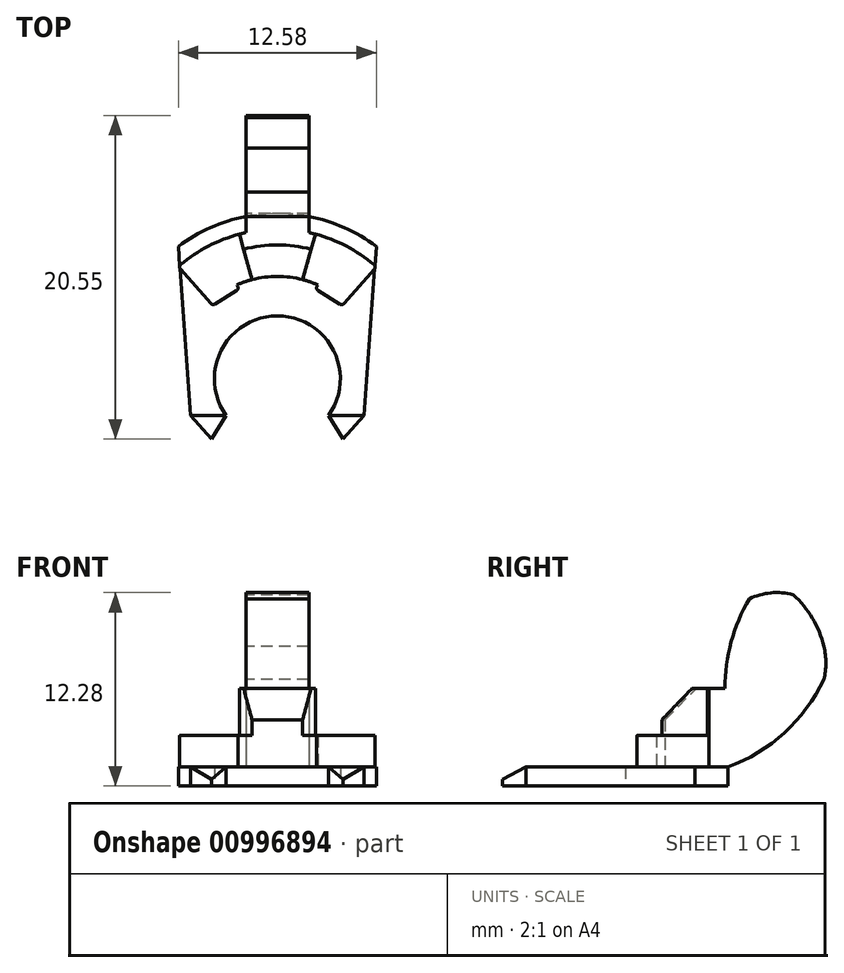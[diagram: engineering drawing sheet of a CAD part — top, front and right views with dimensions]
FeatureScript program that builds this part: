
annotation { "Feature Type Name" : "Feature", "Feature Type Description" : "" }
export const myFeature = defineFeature(function(context is Context, id is Id, definition is map)
    precondition{}
    {
        {
            var Q0;
            Q0=qCreatedBy(makeId("Top.planeOp"),FACE);
            var sketch = newSketch(context, id + "F0", { "sketchPlane" : qUnion([Q0])});
            skLineSegment(sketch, "E0", {"start": v(-7.13, -2.33) * mm, "end": v(-5.5, -2.33) * mm, "construction": true});
            skLineSegment(sketch, "E1", {"start": v(-3.25, -2.33) * mm, "end": v(3.25, -2.33) * mm, "construction": true});
            skLineSegment(sketch, "E2", {"start": v(3.25, -2.33) * mm, "end": v(5.5, -2.33) * mm, "construction": true});
            skArc(sketch, "E3", {"start": v(-7.13, -2.33) * mm, "mid": v(0, -7.5) * mm, "end": v(7.13, -2.33) * mm, "construction": true});
            skArc(sketch, "E4", {"start": v(7.13, -2.33) * mm, "mid": v(7.4, 1.22) * mm, "end": v(6, 4.5) * mm, "construction": true});
            skArc(sketch, "E5", {"start": v(3.25, -2.33) * mm, "mid": v(0, 4) * mm, "end": v(-3.25, -2.33) * mm});
            skArc(sketch, "E6", {"start": v(-3.25, -2.33) * mm, "mid": v(0, -4) * mm, "end": v(3.25, -2.33) * mm, "construction": true});
            skLineSegment(sketch, "E7", {"start": v(-6, 4.5) * mm, "end": v(6, 4.5) * mm, "construction": true});
            skArc(sketch, "E8", {"start": v(6, 4.5) * mm, "mid": v(0, 7.5) * mm, "end": v(-6, 4.5) * mm, "construction": true});
            skArc(sketch, "E9", {"start": v(-6, 4.5) * mm, "mid": v(-7.4, 1.22) * mm, "end": v(-7.13, -2.33) * mm, "construction": true});
            skLineSegment(sketch, "E10", {"start": v(-6.29, 8.41) * mm, "end": v(-5.5, -2.33) * mm});
            skLineSegment(sketch, "E11", {"start": v(6.29, 8.41) * mm, "end": v(5.5, -2.33) * mm});
            skLineSegment(sketch, "E12", {"start": v(-5.5, -2.33) * mm, "end": v(-3.25, -2.33) * mm, "construction": true});
            skLineSegment(sketch, "E13", {"start": v(5.5, -2.33) * mm, "end": v(7.13, -2.33) * mm, "construction": true});
            skLineSegment(sketch, "E14", {"start": v(-5.5, -2.33) * mm, "end": v(-4.18, -3.83) * mm});
            skLineSegment(sketch, "E15", {"start": v(-4.18, -3.83) * mm, "end": v(-3.25, -2.33) * mm});
            skLineSegment(sketch, "E16", {"start": v(3.25, -2.33) * mm, "end": v(4.18, -3.83) * mm});
            skLineSegment(sketch, "E17", {"start": v(4.18, -3.83) * mm, "end": v(5.5, -2.33) * mm});
            skArc(sketch, "E18", {"start": v(-6.29, 8.41) * mm, "mid": v(0, 10.5) * mm, "end": v(6.29, 8.41) * mm});
            skPoint(sketch, "E19", {"position": v(0, 10.5) * mm});
            skPoint(sketch, "E20", {"position": v(0, 7.5) * mm});
            skSolve(sketch);
        }
        {
            var Q0;
            Q0=qSketchRegion(id+"F0",true);
            extrude(context, id + "F1", {"entities" : qUnion([Q0]), "depth" : 1.2 * mm});
        }
        {
            var Q0;
            Q0=qCreatedBy(makeId("Right.planeOp"),FACE);
            var sketch = newSketch(context, id + "F2", { "sketchPlane" : qUnion([Q0])});
            skPoint(sketch, "E21.0", {"position": v(-2.33, 1.2) * mm});
            skLineSegment(sketch, "E22", {"start": v(-2.33, 1.2) * mm, "end": v(-3.83, 0.4) * mm});
            skLineSegment(sketch, "E23", {"start": v(-3.83, 0.4) * mm, "end": v(-3.83, 1.2) * mm});
            skLineSegment(sketch, "E24", {"start": v(-2.33, 1.2) * mm, "end": v(-3.83, 1.2) * mm});
            skSolve(sketch);
        }
        {
            var Q0;
            Q0=qSketchRegion(id+"F2",true);
            extrude(context, id + "F3", {"entities" : qUnion([Q0]), "operationType" : NewBodyOperationType.REMOVE, "endBound" : BoundingType.SYMMETRIC, "oppositeDirection" : true, "depth" : 25 * mm});
        }
        {
            var Q0;
            Q0=makeQuery(id+"F1.opExtrude","CAP_FACE",FACE,{"disambiguationData":[OSD([sQuery(id+"F0.wireOp",EDGE,"E5"),sQuery(id+"F0.wireOp",EDGE,"E10"),sQuery(id+"F0.wireOp",EDGE,"E11"),sQuery(id+"F0.wireOp",EDGE,"E14"),sQuery(id+"F0.wireOp",EDGE,"E15"),sQuery(id+"F0.wireOp",EDGE,"E16"),sQuery(id+"F0.wireOp",EDGE,"E17"),sQuery(id+"F0.wireOp",EDGE,"E18")])],"isStart":false});
            var sketch = newSketch(context, id + "F4", { "sketchPlane" : qUnion([Q0])});
            skArc(sketch, "E25.0", {"start": v(0, 9.5) * mm, "mid": v(-3.27, 8.92) * mm, "end": v(-6.14, 7.25) * mm});
            skArc(sketch, "E26.0", {"start": v(0, 6.5) * mm, "mid": v(-1.31, 6.37) * mm, "end": v(-2.58, 5.97) * mm});
            skPoint(sketch, "E27", {"position": v(0, 9.5) * mm});
            skPoint(sketch, "E28", {"position": v(0, 6.5) * mm});
            skLineSegment(sketch, "E29", {"start": v(-6.3, 7.12) * mm, "end": v(-6.71, 6.74) * mm, "construction": true});
            skLineSegment(sketch, "E30", {"start": v(-6.16, 6.97) * mm, "end": v(-4.3, 4.87) * mm});
            skLineSegment(sketch, "E31", {"start": v(-4.3, 4.87) * mm, "end": v(-4.22, 4.77) * mm});
            skLineSegment(sketch, "E32", {"start": v(-3.96, 4.74) * mm, "end": v(-2.58, 5.6) * mm});
            skLineSegment(sketch, "E33", {"start": v(-2.52, 5.88) * mm, "end": v(-2.58, 5.97) * mm});
            skLineSegment(sketch, "E34", {"start": v(0, 9.5) * mm, "end": v(0, 6.5) * mm, "construction": true});
            skPoint(sketch, "E35.start.orphan", {"position": v(3.7, 8.75) * mm});
            skPoint(sketch, "E36.visualSharp", {"position": v(-6.3, 7.12) * mm});
            skArc(sketch, "E36.filletArc", {"start": v(-6.14, 7.25) * mm, "mid": v(-6.2, 7.11) * mm, "end": v(-6.16, 6.97) * mm});
            skPoint(sketch, "E37.visualSharp", {"position": v(-4.1, 4.65) * mm});
            skArc(sketch, "E37.filletArc", {"start": v(-4.22, 4.77) * mm, "mid": v(-4.1, 4.7) * mm, "end": v(-3.96, 4.74) * mm});
            skPoint(sketch, "E38.visualSharp", {"position": v(-2.41, 5.71) * mm});
            skArc(sketch, "E38.filletArc", {"start": v(-2.58, 5.6) * mm, "mid": v(-2.5, 5.73) * mm, "end": v(-2.52, 5.88) * mm});
            skLineSegment(sketch, "E39.MirrorCS", {"start": v(4.3, 4.87) * mm, "end": v(4.22, 4.77) * mm});
            skArc(sketch, "E40.MirrorCS", {"start": v(4.22, 4.77) * mm, "mid": v(4.1, 4.7) * mm, "end": v(3.96, 4.74) * mm});
            skLineSegment(sketch, "E41.MirrorCS", {"start": v(3.96, 4.74) * mm, "end": v(2.58, 5.6) * mm});
            skPoint(sketch, "E42.MirrorP", {"position": v(4.1, 4.65) * mm});
            skLineSegment(sketch, "E43.MirrorCS", {"start": v(6.16, 6.97) * mm, "end": v(4.3, 4.87) * mm});
            skArc(sketch, "E44.MirrorCS", {"start": v(0, 9.5) * mm, "mid": v(3.27, 8.92) * mm, "end": v(6.14, 7.25) * mm});
            skLineSegment(sketch, "E45.MirrorCS", {"start": v(2.52, 5.88) * mm, "end": v(2.58, 5.97) * mm});
            skArc(sketch, "E46.MirrorCS", {"start": v(2.58, 5.6) * mm, "mid": v(2.5, 5.73) * mm, "end": v(2.52, 5.88) * mm});
            skArc(sketch, "E47.MirrorCS", {"start": v(6.14, 7.25) * mm, "mid": v(6.2, 7.11) * mm, "end": v(6.16, 6.97) * mm});
            skArc(sketch, "E48.MirrorCS", {"start": v(0, 6.5) * mm, "mid": v(1.31, 6.37) * mm, "end": v(2.58, 5.97) * mm});
            skPoint(sketch, "E49.MirrorP", {"position": v(6.3, 7.12) * mm});
            skPoint(sketch, "E50.MirrorP", {"position": v(2.41, 5.71) * mm});
            skLineSegment(sketch, "E51", {"start": v(0, 6.5) * mm, "end": v(0, 9.5) * mm});
            skLineSegment(sketch, "E52", {"start": v(1.6, 6.3) * mm, "end": v(2.41, 9.19) * mm});
            skLineSegment(sketch, "E53.MirrorCS", {"start": v(-1.6, 6.3) * mm, "end": v(-2.41, 9.19) * mm});
            skPoint(sketch, "E54.oppositeSnap0", {"position": v(0, 10.5) * mm});
            skLineSegment(sketch, "E54.top", {"start": v(-2, 10.31) * mm, "end": v(0, 10.31) * mm});
            skLineSegment(sketch, "E54.left", {"start": v(-2, 9.29) * mm, "end": v(-2, 10.31) * mm});
            skLineSegment(sketch, "E54.right", {"start": v(0, 9.49) * mm, "end": v(0, 10.31) * mm});
            skLineSegment(sketch, "E55.MirrorCS", {"start": v(2, 9.29) * mm, "end": v(2, 10.31) * mm});
            skLineSegment(sketch, "E56.MirrorCS", {"start": v(2, 10.31) * mm, "end": v(0, 10.31) * mm});
            skSolve(sketch);
        }
        {
            var Q0;
            Q0=qSketchRegion(id+"F4",true);
            extrude(context, id + "F5", {"entities" : qUnion([Q0]), "operationType" : NewBodyOperationType.ADD, "offsetDistance" : 25 * mm, "depth" : 2 * mm});
        }
        {
            var Q0;
            {var subQ0=sQuery(id+"F4.wireOp",EDGE,"E51");Q0=makeQuery(id+"F4.imprint","IMPRINT",FACE,{"disambiguationData":[TD([[makeQuery(id+"F4.imprint","IMPRINT",EDGE,{"derivedFrom":subQ0}),-1.0]])]});}
            var Q1;
            {var subQ0=sQuery(id+"F4.wireOp",EDGE,"E51");Q1=makeQuery(id+"F4.imprint","IMPRINT",FACE,{"disambiguationData":[TD([[makeQuery(id+"F4.imprint","IMPRINT",EDGE,{"derivedFrom":subQ0}),1.0]])]});}
            extrude(context, id + "F6", {"entities" : qUnion([Q0, Q1]), "operationType" : NewBodyOperationType.ADD, "depth" : 5 * mm, "offsetDistance" : 25 * mm});
        }
        {
            var Q0;
            Q0=makeQuery(id+"F6.opExtrude","CAP_EDGE",EDGE,{"disambiguationData":[OSD([sQuery(id+"F4.wireOp",EDGE,"E26.0"),sQuery(id+"F4.wireOp",EDGE,"E48.MirrorCS")])],"isStart":false});
            chamfer(context, id + "F7", {"entities" : qUnion([Q0]), "width" : 2 * mm, "tangentPropagation" : true});
        }
        {
            var Q0;
            {var subQ3=sQuery(id+"F4.wireOp",EDGE,"E55.MirrorCS");Q0=makeQuery(id+"F4.imprint","IMPRINT",FACE,{"disambiguationData":[TD([[makeQuery(id+"F4.imprint","IMPRINT",EDGE,{"derivedFrom":subQ3}),1.0]])]});}
            var Q1;
            {var subQ4=sQuery(id+"F4.wireOp",EDGE,"E54.top");Q1=makeQuery(id+"F4.imprint","IMPRINT",FACE,{"disambiguationData":[TD([[makeQuery(id+"F4.imprint","IMPRINT",EDGE,{"derivedFrom":subQ4}),-1.0]])]});}
            var Q2;
            Q2=makeQuery(id+"F6.opExtrude","CAP_FACE",FACE,{"disambiguationData":[OSD([sQuery(id+"F4.wireOp",EDGE,"E25.0"),sQuery(id+"F4.wireOp",EDGE,"E26.0"),sQuery(id+"F4.wireOp",EDGE,"E44.MirrorCS"),sQuery(id+"F4.wireOp",EDGE,"E48.MirrorCS"),sQuery(id+"F4.wireOp",EDGE,"E52"),sQuery(id+"F4.wireOp",EDGE,"E53.MirrorCS")])],"isStart":false});
            var Q3;
            Q3=makeQuery(id+"F1.opExtrude","SWEPT_BODY",BODY,{"disambiguationData":[OSD([sQuery(id+"F0.wireOp",EDGE,"E5"),sQuery(id+"F0.wireOp",EDGE,"E10"),sQuery(id+"F0.wireOp",EDGE,"E11"),sQuery(id+"F0.wireOp",EDGE,"E14"),sQuery(id+"F0.wireOp",EDGE,"E15"),sQuery(id+"F0.wireOp",EDGE,"E16"),sQuery(id+"F0.wireOp",EDGE,"E17"),sQuery(id+"F0.wireOp",EDGE,"E18")])]});
            extrude(context, id + "F8", {"entities" : qUnion([Q0, Q1]), "operationType" : NewBodyOperationType.ADD, "endBound" : BoundingType.UP_TO_SURFACE, "depth" : 25 * mm, "endBoundEntityFace" : qUnion([Q2]), "endBoundEntityBody" : qUnion([Q3]), "offsetDistance" : 25 * mm});
        }
        {
            var Q0;
            {var subQ0=sQuery(id+"F4.wireOp",EDGE,"E54.left");Q0=makeQuery(id+"F8.boolean.opBoolean","MERGE",FACE,{"derivedFrom":[makeQuery(id+"F5.opExtrude","SWEPT_FACE",FACE,{"disambiguationData":[OSD([subQ0])]}),makeQuery(id+"F8.opExtrude","SWEPT_FACE",FACE,{"disambiguationData":[OSD([subQ0])]})]});}
            var sketch = newSketch(context, id + "F9", { "sketchPlane" : qUnion([Q0])});
            skLineSegment(sketch, "E57", {"start": v(-10.31, 1.2) * mm, "end": v(-10.5, 1.2) * mm});
            skArc(sketch, "E58", {"start": v(-16.58, 6.76) * mm, "mid": v(-14.09, 3.38) * mm, "end": v(-10.5, 1.2) * mm});
            skArc(sketch, "E59", {"start": v(-16.58, 8.86) * mm, "mid": v(-16.72, 7.8) * mm, "end": v(-16.58, 6.76) * mm});
            skArc(sketch, "E60", {"start": v(-14.64, 12.15) * mm, "mid": v(-15.87, 10.65) * mm, "end": v(-16.58, 8.86) * mm});
            skArc(sketch, "E61", {"start": v(-10.31, 6.2) * mm, "mid": v(-10.7, 9.14) * mm, "end": v(-11.85, 11.88) * mm});
            skArc(sketch, "E62", {"start": v(-11.85, 11.88) * mm, "mid": v(-13.22, 12.26) * mm, "end": v(-14.64, 12.15) * mm});
            skSolve(sketch);
        }
        {
            var Q0;
            Q0=makeQuery(id+"F9.imprint","IMPRINT",FACE,{"disambiguationData":[TD([[makeQuery(id+"F9.imprint","IMPRINT",EDGE,{"derivedFrom":sQuery(id+"F9.wireOp",EDGE,"LY1qM96g-48ux-B85P-QWtM-bPvA0SawryY8")}),-1.0]])]});
            var Q1;
            Q1=makeQuery(id+"F9.imprint","IMPRINT",FACE,{"disambiguationData":[TD([[makeQuery(id+"F9.imprint","IMPRINT",EDGE,{"derivedFrom":sQuery(id+"F9.wireOp",EDGE,"E57")}),-1.0]])]});
            extrude(context, id + "F10", {"entities" : qUnion([Q0, Q1]), "operationType" : NewBodyOperationType.ADD, "oppositeDirection" : true, "depth" : 4 * mm, "offsetDistance" : 25 * mm});
        }
        {
            var Q0;
            {var subQ5=sQuery(id+"F4.wireOp",EDGE,"E44.MirrorCS");var subQ7=sQuery(id+"F4.wireOp",EDGE,"E55.MirrorCS");var subQ8=makeQuery(id+"F4.imprint","INTERSECT",VERTEX,{"derivedFrom":[subQ5,subQ7]});Q0=makeQuery(id+"F4.imprint","IMPRINT",FACE,{"disambiguationData":[TD([[makeQuery(id+"F4.imprint","IMPRINT",EDGE,{"disambiguationData":[TD([[subQ8,-1.0]])],"derivedFrom":subQ7}),1.0]])]});}
            var Q1;
            {var subQ1=sQuery(id+"F4.wireOp",EDGE,"E25.0");var subQ5=sQuery(id+"F4.wireOp",EDGE,"E54.left");var subQ6=makeQuery(id+"F4.imprint","INTERSECT",VERTEX,{"derivedFrom":[subQ1,subQ5]});Q1=makeQuery(id+"F4.imprint","IMPRINT",FACE,{"disambiguationData":[TD([[makeQuery(id+"F4.imprint","IMPRINT",EDGE,{"disambiguationData":[TD([[subQ6,-1.0]])],"derivedFrom":subQ5}),-1.0]])]});}
            var Q2;
            Q2=makeQuery(id+"F6.opExtrude","CAP_FACE",FACE,{"disambiguationData":[OSD([sQuery(id+"F4.wireOp",EDGE,"E25.0"),sQuery(id+"F4.wireOp",EDGE,"E26.0"),sQuery(id+"F4.wireOp",EDGE,"E44.MirrorCS"),sQuery(id+"F4.wireOp",EDGE,"E48.MirrorCS"),sQuery(id+"F4.wireOp",EDGE,"E52"),sQuery(id+"F4.wireOp",EDGE,"E53.MirrorCS")])],"isStart":false});
            extrude(context, id + "F11", {"entities" : qUnion([Q0, Q1]), "operationType" : NewBodyOperationType.ADD, "endBound" : BoundingType.UP_TO_SURFACE, "depth" : 25 * mm, "endBoundEntityFace" : qUnion([Q2]), "offsetDistance" : 25 * mm});
        }
    });
